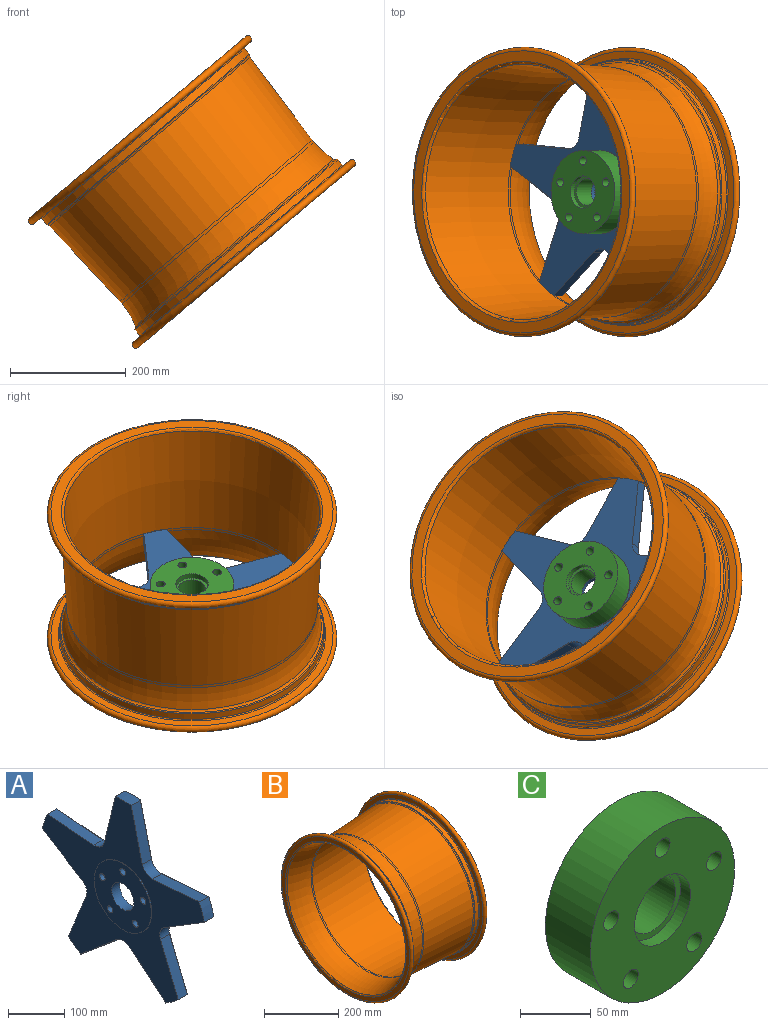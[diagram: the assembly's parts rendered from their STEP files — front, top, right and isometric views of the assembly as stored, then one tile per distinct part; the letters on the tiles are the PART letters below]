
ASSEMBLY  parts=3 mates=5
PART A: 329 faces, bbox 25.4x408.7x389.3 mm
  f0: plane 407.61x388.53mm, normal (1,0,0), area 16823.9mm2, adj f102,f105,f108,f111,f126,f224,f225,f226
  f1: cylinder r=28mm len=56mm, axis (-1,0,0), area 3589mm2, adj f129,f131
  f2: torus R=23mm, axis (1,0,0), area 45.1mm2, adj f3,f4,f18,f26
  f3: cylinder r=2mm len=3.32mm, axis (0,0.31,-0.95), area 8.9mm2, adj f2,f5,f24,f26
  f4: torus R=30mm, axis (1,0,0), area 106.7mm2, adj f2,f6,f23,f26
  f5: torus R=6mm, axis (1,0,0), area 41.3mm2, adj f3,f7,f15,f26
  f6: torus R=23mm, axis (1,0,0), area 45.1mm2, adj f4,f8,f19,f26
  f7: cylinder r=2mm len=101.73mm, axis (0,0.85,0.53), area 371.7mm2, adj f5,f9,f25,f26
  f8: cylinder r=2mm len=3.32mm, axis (0,0.31,-0.95), area 8.9mm2, adj f6,f10,f22,f26
  f9: torus R=6mm, axis (1,0,0), area 29.9mm2, adj f7,f11,f14,f26
  f10: torus R=6mm, axis (1,0,0), area 41.3mm2, adj f8,f12,f16,f26
  f11: torus R=202mm, axis (1,0,0), area 28.8mm2, adj f9,f13,f20,f26
  f12: cylinder r=2mm len=118.12mm, axis (0,-1,-0.08), area 371.7mm2, adj f10,f13,f21,f26
  f13: torus R=6mm, axis (1,0,0), area 29.9mm2, adj f11,f12,f17,f26
  f14: cylinder r=8mm len=9.11mm, axis (1,0,0), area 21mm2, adj f9,f20,f25,f259
  f15: cylinder r=8mm len=11.81mm, axis (-1,0,0), area 29mm2, adj f5,f24,f25,f263
  f16: cylinder r=8mm len=10.45mm, axis (-1,0,0), area 29mm2, adj f10,f21,f22,f256
  f17: cylinder r=8mm len=8.15mm, axis (1,0,0), area 21mm2, adj f13,f20,f21,f255
  f18: cylinder r=25mm len=14.57mm, axis (1,0,0), area 29.6mm2, adj f2,f23,f24,f264
  f19: cylinder r=25mm len=11.94mm, axis (1,0,0), area 29.6mm2, adj f6,f22,f23,f260
  f20: cylinder r=204mm len=8.74mm, axis (1,0,0), area 18.4mm2, adj f11,f14,f17,f257
  f21: plane 117.97x8.92mm, normal (0,0.08,-1), area 236.6mm2, adj f12,f16,f17,f254
  f22: plane 2.7x2mm, normal (0,0.95,0.31), area 5.7mm2, adj f8,f16,f19,f258
  f23: cylinder r=28mm len=29.69mm, axis (1,0,0), area 66.2mm2, adj f4,f18,f19,f262
  f24: plane 2.7x2mm, normal (0,0.95,0.31), area 5.7mm2, adj f3,f15,f18,f265
  f25: plane 100.68x62.12mm, normal (0,-0.53,0.85), area 236.6mm2, adj f7,f14,f15,f261
  f26: plane 132.7x82.52mm, normal (1,0,0), area 5926.3mm2, adj f2,f3,f4,f5,f6,f7,f8,f9
  f27: torus R=23mm, axis (1,0,0), area 45.1mm2, adj f28,f29,f43,f51
  f28: cylinder r=2mm len=3.47mm, axis (0,-0.81,-0.59), area 8.9mm2, adj f27,f30,f49,f51
  f29: torus R=30mm, axis (1,0,0), area 106.7mm2, adj f27,f31,f48,f51
  f30: torus R=6mm, axis (1,0,0), area 41.3mm2, adj f28,f32,f40,f51
  f31: torus R=23mm, axis (1,0,0), area 45.1mm2, adj f29,f33,f44,f51
  f32: cylinder r=2mm len=91.49mm, axis (0,0.76,-0.65), area 371.7mm2, adj f30,f34,f50,f51
  f33: cylinder r=2mm len=3.47mm, axis (0,-0.81,-0.59), area 8.9mm2, adj f31,f35,f47,f51
  f34: torus R=6mm, axis (1,0,0), area 29.9mm2, adj f32,f36,f39,f51
  f35: torus R=6mm, axis (1,0,0), area 41.3mm2, adj f33,f37,f41,f51
  f36: torus R=202mm, axis (1,0,0), area 28.8mm2, adj f34,f38,f45,f51
  f37: cylinder r=2mm len=110.2mm, axis (0,-0.38,0.93), area 371.7mm2, adj f35,f38,f46,f51
  f38: torus R=6mm, axis (1,0,0), area 29.9mm2, adj f36,f37,f42,f51
  f39: cylinder r=8mm len=9.73mm, axis (1,0,0), area 21mm2, adj f34,f45,f50,f271
  f40: cylinder r=8mm len=12.57mm, axis (-1,0,0), area 29mm2, adj f30,f49,f50,f267
  f41: cylinder r=8mm len=12.1mm, axis (-1,0,0), area 29mm2, adj f35,f46,f47,f276
  f42: cylinder r=8mm len=9.4mm, axis (1,0,0), area 21mm2, adj f38,f45,f46,f275
  f43: cylinder r=25mm len=13.77mm, axis (1,0,0), area 29.6mm2, adj f27,f48,f49,f268
  f44: cylinder r=25mm len=11.63mm, axis (1,0,0), area 29.6mm2, adj f31,f47,f48,f272
  f45: cylinder r=204mm len=7.44mm, axis (1,0,0), area 18.4mm2, adj f36,f39,f42,f273
  f46: plane 109.44x44.94mm, normal (0,-0.93,-0.38), area 236.6mm2, adj f37,f41,f42,f277
  f47: plane 2.3x2mm, normal (0,0.59,-0.81), area 5.7mm2, adj f33,f41,f44,f274
  f48: cylinder r=28mm len=25.26mm, axis (1,0,0), area 66.2mm2, adj f29,f43,f44,f270
  f49: plane 2.3x2mm, normal (0,0.59,-0.81), area 5.7mm2, adj f28,f40,f43,f266
  f50: plane 90.19x76.56mm, normal (0,0.65,0.76), area 236.6mm2, adj f32,f39,f40,f269
  f51: plane 126.63x109.34mm, normal (1,0,0), area 5926.3mm2, adj f27,f28,f29,f30,f31,f32,f33,f34
  f52: torus R=23mm, axis (1,0,0), area 45.1mm2, adj f53,f54,f68,f76
  f53: cylinder r=2mm len=3.47mm, axis (0,-0.81,0.59), area 8.9mm2, adj f52,f55,f74,f76
  f54: torus R=30mm, axis (1,0,0), area 106.7mm2, adj f52,f56,f73,f76
  f55: torus R=6mm, axis (1,0,0), area 41.3mm2, adj f53,f57,f65,f76
  f56: torus R=23mm, axis (1,0,0), area 45.1mm2, adj f54,f58,f69,f76
  f57: cylinder r=2mm len=110.2mm, axis (0,-0.38,-0.93), area 371.7mm2, adj f55,f59,f75,f76
  f58: cylinder r=2mm len=3.47mm, axis (0,-0.81,0.59), area 8.9mm2, adj f56,f60,f72,f76
  f59: torus R=6mm, axis (1,0,0), area 29.9mm2, adj f57,f61,f64,f76
  f60: torus R=6mm, axis (1,0,0), area 41.3mm2, adj f58,f62,f66,f76
  f61: torus R=202mm, axis (1,0,0), area 28.8mm2, adj f59,f63,f70,f76
  f62: cylinder r=2mm len=91.49mm, axis (0,0.76,0.65), area 371.7mm2, adj f60,f63,f71,f76
  f63: torus R=6mm, axis (1,0,0), area 29.9mm2, adj f61,f62,f67,f76
  f64: cylinder r=8mm len=9.4mm, axis (1,0,0), area 21mm2, adj f59,f70,f75,f279
  f65: cylinder r=8mm len=12.1mm, axis (-1,0,0), area 29mm2, adj f55,f74,f75,f280
  f66: cylinder r=8mm len=12.57mm, axis (-1,0,0), area 29mm2, adj f60,f71,f72,f287
  f67: cylinder r=8mm len=9.73mm, axis (1,0,0), area 21mm2, adj f63,f70,f71,f283
  f68: cylinder r=25mm len=11.63mm, axis (1,0,0), area 29.6mm2, adj f52,f73,f74,f284
  f69: cylinder r=25mm len=13.77mm, axis (1,0,0), area 29.6mm2, adj f56,f72,f73,f288
  f70: cylinder r=204mm len=7.44mm, axis (1,0,0), area 18.4mm2, adj f61,f64,f67,f281
  f71: plane 90.19x76.56mm, normal (0,-0.65,0.76), area 236.6mm2, adj f62,f66,f67,f285
  f72: plane 2.3x2mm, normal (0,-0.59,-0.81), area 5.7mm2, adj f58,f66,f69,f289
  f73: cylinder r=28mm len=25.26mm, axis (1,0,0), area 66.2mm2, adj f54,f68,f69,f286
  f74: plane 2.3x2mm, normal (0,-0.59,-0.81), area 5.7mm2, adj f53,f65,f68,f282
  f75: plane 109.44x44.94mm, normal (0,0.93,-0.38), area 236.6mm2, adj f57,f64,f65,f278
  f76: plane 126.63x109.34mm, normal (1,0,0), area 5926.3mm2, adj f52,f53,f54,f55,f56,f57,f58,f59
  f77: torus R=23mm, axis (1,0,0), area 45.1mm2, adj f78,f79,f93,f101
  f78: cylinder r=2mm len=3.32mm, axis (0,0.31,0.95), area 8.9mm2, adj f77,f80,f99,f101
  f79: torus R=30mm, axis (1,0,0), area 106.7mm2, adj f77,f81,f98,f101
  f80: torus R=6mm, axis (1,0,0), area 41.3mm2, adj f78,f82,f90,f101
  f81: torus R=23mm, axis (1,0,0), area 45.1mm2, adj f79,f83,f94,f101
  f82: cylinder r=2mm len=118.12mm, axis (0,-1,0.08), area 371.7mm2, adj f80,f84,f100,f101
  f83: cylinder r=2mm len=3.32mm, axis (0,0.31,0.95), area 8.9mm2, adj f81,f85,f97,f101
  f84: torus R=6mm, axis (1,0,0), area 29.9mm2, adj f82,f86,f89,f101
  f85: torus R=6mm, axis (1,0,0), area 41.3mm2, adj f83,f87,f91,f101
  f86: torus R=202mm, axis (1,0,0), area 28.8mm2, adj f84,f88,f95,f101
  f87: cylinder r=2mm len=101.73mm, axis (0,0.85,-0.53), area 371.7mm2, adj f85,f88,f96,f101
  f88: torus R=6mm, axis (1,0,0), area 29.9mm2, adj f86,f87,f92,f101
  f89: cylinder r=8mm len=8.15mm, axis (1,0,0), area 21mm2, adj f84,f95,f100,f291
  f90: cylinder r=8mm len=10.45mm, axis (-1,0,0), area 29mm2, adj f80,f99,f100,f292
  f91: cylinder r=8mm len=11.81mm, axis (-1,0,0), area 29mm2, adj f85,f96,f97,f299
  f92: cylinder r=8mm len=9.11mm, axis (1,0,0), area 21mm2, adj f88,f95,f96,f295
  f93: cylinder r=25mm len=11.94mm, axis (1,0,0), area 29.6mm2, adj f77,f98,f99,f296
  f94: cylinder r=25mm len=14.57mm, axis (1,0,0), area 29.6mm2, adj f81,f97,f98,f300
  f95: cylinder r=204mm len=8.74mm, axis (1,0,0), area 18.4mm2, adj f86,f89,f92,f293
  f96: plane 100.68x62.12mm, normal (0,0.53,0.85), area 236.6mm2, adj f87,f91,f92,f297
  f97: plane 2.7x2mm, normal (0,-0.95,0.31), area 5.7mm2, adj f83,f91,f94,f301
  f98: cylinder r=28mm len=29.69mm, axis (1,0,0), area 66.2mm2, adj f79,f93,f94,f298
  f99: plane 2.7x2mm, normal (0,-0.95,0.31), area 5.7mm2, adj f78,f90,f93,f294
  f100: plane 117.97x8.92mm, normal (0,-0.08,-1), area 236.6mm2, adj f82,f89,f90,f290
  f101: plane 132.7x82.52mm, normal (1,0,0), area 5926.3mm2, adj f77,f78,f79,f80,f81,f82,f83,f84
  f102: cylinder r=209mm len=32.36mm, axis (-1,0,0), area 960.8mm2, adj f0,f104,f106,f127,f168,f316,f317
  f103: plane 100.38x61.94mm, normal (0,0.53,-0.85), area 2712.9mm2, adj f126,f127,f161,f314
  f104: plane 109.11x44.81mm, normal (0,0.93,0.38), area 2712.9mm2, adj f102,f127,f161,f316
  f105: cylinder r=209mm len=32.36mm, axis (-1,0,0), area 960.8mm2, adj f0,f107,f109,f127,f166,f319,f320
  f106: plane 89.92x76.33mm, normal (0,-0.65,-0.76), area 2595mm2, adj f102,f162,f168,f317
  f107: plane 89.92x76.33mm, normal (0,0.65,-0.76), area 2595mm2, adj f105,f162,f166,f319
  f108: cylinder r=209mm len=38.04mm, axis (-1,0,0), area 961mm2, adj f0,f110,f112,f127,f322,f323
  f109: plane 109.11x44.81mm, normal (0,-0.93,0.38), area 2712.9mm2, adj f105,f127,f163,f320
  f110: plane 100.38x61.94mm, normal (0,-0.53,-0.85), area 2712.9mm2, adj f108,f127,f163,f322
  f111: cylinder r=209mm len=40mm, axis (-1,0,0), area 961mm2, adj f0,f113,f127,f134,f325,f326
  f112: plane 117.62x23mm, normal (0,0.08,1), area 2712.9mm2, adj f108,f127,f164,f323
  f113: plane 114.61x27.88mm, normal (0,-0.97,0.24), area 2712.9mm2, adj f111,f127,f164,f325
  f114: cylinder r=18mm len=22.13mm, axis (-1,0,0), area 50.6mm2, adj f192,f193,f214,f243
  f115: cone r=7mm half-angle=30deg, axis (1,0,0), area 596.9mm2, adj f116,f131
  f116: cylinder r=7mm len=14mm, axis (-1,0,0), area 516.3mm2, adj f115,f129
  f117: cylinder r=18mm len=18.82mm, axis (-1,0,0), area 50.6mm2, adj f190,f191,f221,f252
  f118: cone r=7mm half-angle=30deg, axis (1,0,0), area 596.9mm2, adj f119,f131
  f119: cylinder r=7mm len=14mm, axis (-1,0,0), area 516.3mm2, adj f118,f129
  f120: cylinder r=18mm len=18.82mm, axis (-1,0,0), area 50.6mm2, adj f188,f189,f209,f240
  f121: cone r=7mm half-angle=30deg, axis (1,0,0), area 596.9mm2, adj f122,f131
  f122: cylinder r=7mm len=14mm, axis (-1,0,0), area 516.3mm2, adj f121,f129
  f123: cylinder r=18mm len=22.13mm, axis (-1,0,0), area 50.6mm2, adj f186,f187,f197,f228
  f124: cone r=7mm half-angle=30deg, axis (1,0,0), area 596.9mm2, adj f125,f131
  f125: cylinder r=7mm len=14mm, axis (-1,0,0), area 516.3mm2, adj f124,f129
  f126: cylinder r=209mm len=38.04mm, axis (-1,0,0), area 961mm2, adj f0,f103,f127,f135,f314,f328
  f127: plane 408.08x388.53mm, normal (-1,0,0), area 52573.4mm2, adj f102,f103,f104,f105,f108,f109,f110,f111
  f128: cylinder r=72mm len=144mm, axis (-1,0,0), area 633.3mm2, adj f127,f129
  f129: plane 144x144mm, normal (-1,0,0), area 13053.3mm2, adj f1,f116,f119,f122,f125,f128,f133
  f130: cylinder r=18mm len=23.26mm, axis (-1,0,0), area 50.6mm2, adj f184,f185,f202,f231
  f131: plane 143.04x139.91mm, normal (1,0,0), area 9784mm2, adj f1,f115,f118,f121,f124,f132,f194,f195
  f132: cone r=7mm half-angle=30deg, axis (1,0,0), area 596.9mm2, adj f131,f133
  f133: cylinder r=7mm len=14mm, axis (-1,0,0), area 516.3mm2, adj f129,f132
  f134: plane 114.61x27.88mm, normal (0,0.97,0.24), area 2712.9mm2, adj f111,f127,f165,f326
  f135: plane 117.62x23mm, normal (0,-0.08,1), area 2712.9mm2, adj f126,f127,f165,f328
  f136: cylinder r=204mm len=9.19mm, axis (1,0,0), area 18.4mm2, adj f145,f148,f158,f305
  f137: plane 114.95x27.97mm, normal (0,0.97,-0.24), area 236.6mm2, adj f145,f146,f159,f309
  f138: plane 2.84x2mm, normal (0,0,1), area 5.7mm2, adj f143,f146,f155,f313
  f139: cylinder r=28mm len=31.22mm, axis (1,0,0), area 66.2mm2, adj f143,f144,f151,f310
  f140: plane 2.84x2mm, normal (0,0,1), area 5.7mm2, adj f144,f147,f150,f306
  f141: plane 114.95x27.97mm, normal (0,-0.97,-0.24), area 236.6mm2, adj f147,f148,f154,f302
  f142: plane 127x76.77mm, normal (1,0,0), area 5926.3mm2, adj f149,f150,f151,f152,f153,f154,f155,f156
  f143: cylinder r=25mm len=13.94mm, axis (1,0,0), area 29.6mm2, adj f138,f139,f153,f312
  f144: cylinder r=25mm len=13.94mm, axis (1,0,0), area 29.6mm2, adj f139,f140,f149,f308
  f145: cylinder r=8mm len=7.59mm, axis (1,0,0), area 21mm2, adj f136,f137,f160,f307
  f146: cylinder r=8mm len=9.89mm, axis (-1,0,0), area 29mm2, adj f137,f138,f157,f311
  f147: cylinder r=8mm len=9.89mm, axis (-1,0,0), area 29mm2, adj f140,f141,f152,f304
  f148: cylinder r=8mm len=7.59mm, axis (1,0,0), area 21mm2, adj f136,f141,f156,f303
  f149: torus R=23mm, axis (1,0,0), area 45.1mm2, adj f142,f144,f150,f151
  f150: cylinder r=2mm len=2.84mm, axis (0,1,0), area 8.9mm2, adj f140,f142,f149,f152
  f151: torus R=30mm, axis (1,0,0), area 106.7mm2, adj f139,f142,f149,f153
  f152: torus R=6mm, axis (1,0,0), area 41.3mm2, adj f142,f147,f150,f154
  f153: torus R=23mm, axis (1,0,0), area 45.1mm2, adj f142,f143,f151,f155
  f154: cylinder r=2mm len=115.42mm, axis (0,-0.24,0.97), area 371.7mm2, adj f141,f142,f152,f156
  f155: cylinder r=2mm len=2.84mm, axis (0,1,0), area 8.9mm2, adj f138,f142,f153,f157
  f156: torus R=6mm, axis (1,0,0), area 29.9mm2, adj f142,f148,f154,f158
  f157: torus R=6mm, axis (1,0,0), area 41.3mm2, adj f142,f146,f155,f159
  f158: torus R=202mm, axis (1,0,0), area 28.8mm2, adj f136,f142,f156,f160
  f159: cylinder r=2mm len=115.42mm, axis (0,-0.24,-0.97), area 371.7mm2, adj f137,f142,f157,f160
  f160: torus R=6mm, axis (1,0,0), area 29.9mm2, adj f142,f145,f158,f159
  f161: cylinder r=25mm len=30.77mm, axis (1,0,0), area 809.4mm2, adj f103,f104,f127,f315
  f162: cylinder r=25mm len=32.36mm, axis (1,0,0), area 774.2mm2, adj f106,f107,f167,f318
  f163: cylinder r=25mm len=30.77mm, axis (1,0,0), area 809.4mm2, adj f109,f110,f127,f321
  f164: cylinder r=25mm len=26.18mm, axis (1,0,0), area 809.4mm2, adj f112,f113,f127,f324
  f165: cylinder r=25mm len=26.18mm, axis (1,0,0), area 809.4mm2, adj f127,f134,f135,f327
  f166: cylinder r=1mm len=90.83mm, axis (0,-0.76,-0.65), area 185.5mm2, adj f105,f107,f127,f167
  f167: torus R=26mm, axis (1,0,0), area 56.1mm2, adj f127,f162,f166,f168
  f168: cylinder r=1mm len=90.83mm, axis (0,-0.76,0.65), area 185.5mm2, adj f102,f106,f127,f167
  f169: plane 12.5x2mm, normal (0,0,-1), area 25mm2, adj f179,f184,f198,f227
  f170: plane 11.89x3.86mm, normal (0,0.95,-0.31), area 25mm2, adj f179,f187,f194,f224
  f171: plane 11.89x3.86mm, normal (0,0.95,-0.31), area 25mm2, adj f180,f186,f201,f232
  f172: plane 10.11x7.35mm, normal (0,0.59,0.81), area 25mm2, adj f180,f189,f205,f236
  f173: plane 10.11x7.35mm, normal (0,0.59,0.81), area 25mm2, adj f181,f188,f213,f244
  f174: plane 10.11x7.35mm, normal (0,-0.59,0.81), area 25mm2, adj f181,f191,f217,f248
  f175: plane 10.11x7.35mm, normal (0,-0.59,0.81), area 25mm2, adj f182,f190,f222,f251
  f176: plane 11.89x3.86mm, normal (0,-0.95,-0.31), area 25mm2, adj f182,f193,f218,f247
  f177: plane 11.89x3.86mm, normal (0,-0.95,-0.31), area 25mm2, adj f183,f192,f210,f239
  f178: plane 12.5x2mm, normal (0,0,-1), area 25mm2, adj f183,f185,f206,f235
  f179: cylinder r=12mm len=11.41mm, axis (1,0,0), area 30.2mm2, adj f169,f170,f196,f225
  f180: cylinder r=12mm len=13.42mm, axis (1,0,0), area 30.2mm2, adj f171,f172,f203,f234
  f181: cylinder r=12mm len=14.11mm, axis (1,0,0), area 30.2mm2, adj f173,f174,f215,f246
  f182: cylinder r=12mm len=13.42mm, axis (1,0,0), area 30.2mm2, adj f175,f176,f220,f249
  f183: cylinder r=12mm len=11.41mm, axis (1,0,0), area 30.2mm2, adj f177,f178,f208,f237
  f184: cylinder r=20mm len=12.92mm, axis (-1,0,0), area 28.1mm2, adj f130,f169,f200,f229
  f185: cylinder r=20mm len=12.92mm, axis (-1,0,0), area 28.1mm2, adj f130,f178,f204,f233
  f186: cylinder r=20mm len=13.76mm, axis (-1,0,0), area 28.1mm2, adj f123,f171,f199,f230
  f187: cylinder r=20mm len=10.83mm, axis (-1,0,0), area 28.1mm2, adj f123,f170,f195,f226
  f188: cylinder r=20mm len=13.24mm, axis (-1,0,0), area 28.1mm2, adj f120,f173,f211,f242
  f189: cylinder r=20mm len=11.43mm, axis (-1,0,0), area 28.1mm2, adj f120,f172,f207,f238
  f190: cylinder r=20mm len=11.43mm, axis (-1,0,0), area 28.1mm2, adj f117,f175,f223,f253
  f191: cylinder r=20mm len=13.24mm, axis (-1,0,0), area 28.1mm2, adj f117,f174,f219,f250
  f192: cylinder r=20mm len=10.83mm, axis (-1,0,0), area 28.1mm2, adj f114,f177,f212,f241
  f193: cylinder r=20mm len=13.76mm, axis (-1,0,0), area 28.1mm2, adj f114,f176,f216,f245
  f194: cylinder r=2mm len=12.5mm, axis (0,0.31,0.95), area 39.3mm2, adj f131,f170,f195,f196
  f195: torus R=22mm, axis (-1,0,0), area 45.8mm2, adj f131,f187,f194,f197
  f196: torus R=10mm, axis (-1,0,0), area 44.5mm2, adj f131,f179,f194,f198
  f197: torus R=16mm, axis (-1,0,0), area 76.3mm2, adj f123,f131,f195,f199
  f198: cylinder r=2mm len=12.5mm, axis (0,1,0), area 39.3mm2, adj f131,f169,f196,f200
  f199: torus R=22mm, axis (-1,0,0), area 45.8mm2, adj f131,f186,f197,f201
  f200: torus R=22mm, axis (-1,0,0), area 45.8mm2, adj f131,f184,f198,f202
  f201: cylinder r=2mm len=12.5mm, axis (0,0.31,0.95), area 39.3mm2, adj f131,f171,f199,f203
  f202: torus R=16mm, axis (-1,0,0), area 76.3mm2, adj f130,f131,f200,f204
  f203: torus R=10mm, axis (-1,0,0), area 44.5mm2, adj f131,f180,f201,f205
  f204: torus R=22mm, axis (-1,0,0), area 45.8mm2, adj f131,f185,f202,f206
  f205: cylinder r=2mm len=11.29mm, axis (0,-0.81,0.59), area 39.3mm2, adj f131,f172,f203,f207
  f206: cylinder r=2mm len=12.5mm, axis (0,1,0), area 39.3mm2, adj f131,f178,f204,f208
  f207: torus R=22mm, axis (-1,0,0), area 45.8mm2, adj f131,f189,f205,f209
  f208: torus R=10mm, axis (-1,0,0), area 44.5mm2, adj f131,f183,f206,f210
  f209: torus R=16mm, axis (-1,0,0), area 76.3mm2, adj f120,f131,f207,f211
  f210: cylinder r=2mm len=12.5mm, axis (0,0.31,-0.95), area 39.3mm2, adj f131,f177,f208,f212
  f211: torus R=22mm, axis (-1,0,0), area 45.8mm2, adj f131,f188,f209,f213
  f212: torus R=22mm, axis (-1,0,0), area 45.8mm2, adj f131,f192,f210,f214
  f213: cylinder r=2mm len=11.29mm, axis (0,-0.81,0.59), area 39.3mm2, adj f131,f173,f211,f215
  f214: torus R=16mm, axis (-1,0,0), area 76.3mm2, adj f114,f131,f212,f216
  f215: torus R=10mm, axis (-1,0,0), area 44.5mm2, adj f131,f181,f213,f217
  f216: torus R=22mm, axis (-1,0,0), area 45.8mm2, adj f131,f193,f214,f218
  f217: cylinder r=2mm len=11.29mm, axis (0,-0.81,-0.59), area 39.3mm2, adj f131,f174,f215,f219
  f218: cylinder r=2mm len=12.5mm, axis (0,0.31,-0.95), area 39.3mm2, adj f131,f176,f216,f220
  f219: torus R=22mm, axis (-1,0,0), area 45.8mm2, adj f131,f191,f217,f221
  f220: torus R=10mm, axis (-1,0,0), area 44.5mm2, adj f131,f182,f218,f222
  f221: torus R=16mm, axis (-1,0,0), area 76.3mm2, adj f117,f131,f219,f223
  f222: cylinder r=2mm len=11.29mm, axis (0,-0.81,-0.59), area 39.3mm2, adj f131,f175,f220,f223
  f223: torus R=22mm, axis (-1,0,0), area 45.8mm2, adj f131,f190,f221,f222
  f224: cylinder r=1mm len=12.2mm, axis (0,-0.31,-0.95), area 19.6mm2, adj f0,f170,f225,f226
  f225: torus R=13mm, axis (-1,0,0), area 24.4mm2, adj f0,f179,f224,f227
  f226: torus R=19mm, axis (-1,0,0), area 21.7mm2, adj f0,f187,f224,f228
  f227: cylinder r=1mm len=12.5mm, axis (0,-1,0), area 19.6mm2, adj f0,f169,f225,f229
  f228: torus R=19mm, axis (-1,0,0), area 40.5mm2, adj f0,f123,f226,f230
  f229: torus R=19mm, axis (-1,0,0), area 21.7mm2, adj f0,f184,f227,f231
  f230: torus R=19mm, axis (-1,0,0), area 21.7mm2, adj f0,f186,f228,f232
  f231: torus R=19mm, axis (-1,0,0), area 40.5mm2, adj f0,f130,f229,f233
  f232: cylinder r=1mm len=12.2mm, axis (0,-0.31,-0.95), area 19.6mm2, adj f0,f171,f230,f234
  f233: torus R=19mm, axis (-1,0,0), area 21.7mm2, adj f0,f185,f231,f235
  f234: torus R=13mm, axis (-1,0,0), area 24.4mm2, adj f0,f180,f232,f236
  f235: cylinder r=1mm len=12.5mm, axis (0,-1,0), area 19.6mm2, adj f0,f178,f233,f237
  f236: cylinder r=1mm len=10.7mm, axis (0,0.81,-0.59), area 19.6mm2, adj f0,f172,f234,f238
  f237: torus R=13mm, axis (-1,0,0), area 24.4mm2, adj f0,f183,f235,f239
  f238: torus R=19mm, axis (-1,0,0), area 21.7mm2, adj f0,f189,f236,f240
  f239: cylinder r=1mm len=12.2mm, axis (0,-0.31,0.95), area 19.6mm2, adj f0,f177,f237,f241
  f240: torus R=19mm, axis (-1,0,0), area 40.5mm2, adj f0,f120,f238,f242
  f241: torus R=19mm, axis (-1,0,0), area 21.7mm2, adj f0,f192,f239,f243
  f242: torus R=19mm, axis (-1,0,0), area 21.7mm2, adj f0,f188,f240,f244
  f243: torus R=19mm, axis (-1,0,0), area 40.5mm2, adj f0,f114,f241,f245
  f244: cylinder r=1mm len=10.7mm, axis (0,0.81,-0.59), area 19.6mm2, adj f0,f173,f242,f246
  f245: torus R=19mm, axis (-1,0,0), area 21.7mm2, adj f0,f193,f243,f247
  f246: torus R=13mm, axis (-1,0,0), area 24.4mm2, adj f0,f181,f244,f248
  f247: cylinder r=1mm len=12.2mm, axis (0,-0.31,0.95), area 19.6mm2, adj f0,f176,f245,f249
  f248: cylinder r=1mm len=10.7mm, axis (0,0.81,0.59), area 19.6mm2, adj f0,f174,f246,f250
  f249: torus R=13mm, axis (-1,0,0), area 24.4mm2, adj f0,f182,f247,f251
  f250: torus R=19mm, axis (-1,0,0), area 21.7mm2, adj f0,f191,f248,f252
  f251: cylinder r=1mm len=10.7mm, axis (0,0.81,0.59), area 19.6mm2, adj f0,f175,f249,f253
  f252: torus R=19mm, axis (-1,0,0), area 40.5mm2, adj f0,f117,f250,f253
  f253: torus R=19mm, axis (-1,0,0), area 21.7mm2, adj f0,f190,f251,f252
  f254: cylinder r=1mm len=118.04mm, axis (0,-1,-0.08), area 185.8mm2, adj f0,f21,f255,f256
  f255: torus R=9mm, axis (-1,0,0), area 17.2mm2, adj f0,f17,f254,f257
  f256: torus R=9mm, axis (-1,0,0), area 23.8mm2, adj f0,f16,f254,f258
  f257: torus R=205mm, axis (-1,0,0), area 14.5mm2, adj f0,f20,f255,f259
  f258: cylinder r=1mm len=3.01mm, axis (0,0.31,-0.95), area 4.5mm2, adj f0,f22,f256,f260
  f259: torus R=9mm, axis (-1,0,0), area 17.2mm2, adj f0,f14,f257,f261
  f260: torus R=26mm, axis (-1,0,0), area 23.6mm2, adj f0,f19,f258,f262
  f261: cylinder r=1mm len=101.21mm, axis (0,0.85,0.53), area 185.8mm2, adj f0,f25,f259,f263
  f262: torus R=27mm, axis (-1,0,0), area 51.3mm2, adj f0,f23,f260,f264
  f263: torus R=9mm, axis (-1,0,0), area 23.8mm2, adj f0,f15,f261,f265
  f264: torus R=26mm, axis (-1,0,0), area 23.6mm2, adj f0,f18,f262,f265
  f265: cylinder r=1mm len=3.01mm, axis (0,0.31,-0.95), area 4.5mm2, adj f0,f24,f263,f264
  f266: cylinder r=1mm len=2.88mm, axis (0,-0.81,-0.59), area 4.5mm2, adj f0,f49,f267,f268
  f267: torus R=9mm, axis (-1,0,0), area 23.8mm2, adj f0,f40,f266,f269
  f268: torus R=26mm, axis (-1,0,0), area 23.6mm2, adj f0,f43,f266,f270
  f269: cylinder r=1mm len=90.84mm, axis (0,0.76,-0.65), area 185.8mm2, adj f0,f50,f267,f271
  f270: torus R=27mm, axis (-1,0,0), area 51.3mm2, adj f0,f48,f268,f272
  f271: torus R=9mm, axis (-1,0,0), area 17.2mm2, adj f0,f39,f269,f273
  f272: torus R=26mm, axis (-1,0,0), area 23.6mm2, adj f0,f44,f270,f274
  f273: torus R=205mm, axis (-1,0,0), area 14.5mm2, adj f0,f45,f271,f275
  f274: cylinder r=1mm len=2.88mm, axis (0,-0.81,-0.59), area 4.5mm2, adj f0,f47,f272,f276
  f275: torus R=9mm, axis (-1,0,0), area 17.2mm2, adj f0,f42,f273,f277
  f276: torus R=9mm, axis (-1,0,0), area 23.8mm2, adj f0,f41,f274,f277
  f277: cylinder r=1mm len=109.82mm, axis (0,-0.38,0.93), area 185.8mm2, adj f0,f46,f275,f276
  f278: cylinder r=1mm len=109.82mm, axis (0,-0.38,-0.93), area 185.8mm2, adj f0,f75,f279,f280
  f279: torus R=9mm, axis (-1,0,0), area 17.2mm2, adj f0,f64,f278,f281
  f280: torus R=9mm, axis (-1,0,0), area 23.8mm2, adj f0,f65,f278,f282
  f281: torus R=205mm, axis (-1,0,0), area 14.5mm2, adj f0,f70,f279,f283
  f282: cylinder r=1mm len=2.88mm, axis (0,-0.81,0.59), area 4.5mm2, adj f0,f74,f280,f284
  f283: torus R=9mm, axis (-1,0,0), area 17.2mm2, adj f0,f67,f281,f285
  f284: torus R=26mm, axis (-1,0,0), area 23.6mm2, adj f0,f68,f282,f286
  f285: cylinder r=1mm len=90.84mm, axis (0,0.76,0.65), area 185.8mm2, adj f0,f71,f283,f287
  f286: torus R=27mm, axis (-1,0,0), area 51.3mm2, adj f0,f73,f284,f288
  f287: torus R=9mm, axis (-1,0,0), area 23.8mm2, adj f0,f66,f285,f289
  f288: torus R=26mm, axis (-1,0,0), area 23.6mm2, adj f0,f69,f286,f289
  f289: cylinder r=1mm len=2.88mm, axis (0,-0.81,0.59), area 4.5mm2, adj f0,f72,f287,f288
  f290: cylinder r=1mm len=118.04mm, axis (0,-1,0.08), area 185.8mm2, adj f0,f100,f291,f292
  f291: torus R=9mm, axis (-1,0,0), area 17.2mm2, adj f0,f89,f290,f293
  f292: torus R=9mm, axis (-1,0,0), area 23.8mm2, adj f0,f90,f290,f294
  f293: torus R=205mm, axis (-1,0,0), area 14.5mm2, adj f0,f95,f291,f295
  f294: cylinder r=1mm len=3.01mm, axis (0,0.31,0.95), area 4.5mm2, adj f0,f99,f292,f296
  f295: torus R=9mm, axis (-1,0,0), area 17.2mm2, adj f0,f92,f293,f297
  f296: torus R=26mm, axis (-1,0,0), area 23.6mm2, adj f0,f93,f294,f298
  f297: cylinder r=1mm len=101.21mm, axis (0,0.85,-0.53), area 185.8mm2, adj f0,f96,f295,f299
  f298: torus R=27mm, axis (-1,0,0), area 51.3mm2, adj f0,f98,f296,f300
  f299: torus R=9mm, axis (-1,0,0), area 23.8mm2, adj f0,f91,f297,f301
  f300: torus R=26mm, axis (-1,0,0), area 23.6mm2, adj f0,f94,f298,f301
  f301: cylinder r=1mm len=3.01mm, axis (0,0.31,0.95), area 4.5mm2, adj f0,f97,f299,f300
  f302: cylinder r=1mm len=115.19mm, axis (0,-0.24,0.97), area 185.8mm2, adj f0,f141,f303,f304
  f303: torus R=9mm, axis (-1,0,0), area 17.2mm2, adj f0,f148,f302,f305
  f304: torus R=9mm, axis (-1,0,0), area 23.8mm2, adj f0,f147,f302,f306
  f305: torus R=205mm, axis (-1,0,0), area 14.5mm2, adj f0,f136,f303,f307
  f306: cylinder r=1mm len=2.84mm, axis (0,1,0), area 4.5mm2, adj f0,f140,f304,f308
  f307: torus R=9mm, axis (-1,0,0), area 17.2mm2, adj f0,f145,f305,f309
  f308: torus R=26mm, axis (-1,0,0), area 23.6mm2, adj f0,f144,f306,f310
  f309: cylinder r=1mm len=115.19mm, axis (0,-0.24,-0.97), area 185.8mm2, adj f0,f137,f307,f311
  f310: torus R=27mm, axis (-1,0,0), area 51.3mm2, adj f0,f139,f308,f312
  f311: torus R=9mm, axis (-1,0,0), area 23.8mm2, adj f0,f146,f309,f313
  f312: torus R=26mm, axis (-1,0,0), area 23.6mm2, adj f0,f143,f310,f313
  f313: cylinder r=1mm len=2.84mm, axis (0,1,0), area 4.5mm2, adj f0,f138,f311,f312
  f314: cylinder r=1mm len=101.2mm, axis (0,0.85,0.53), area 185.5mm2, adj f0,f103,f126,f315
  f315: torus R=26mm, axis (-1,0,0), area 56.1mm2, adj f0,f161,f314,f316
  f316: cylinder r=1mm len=109.81mm, axis (0,-0.38,0.93), area 185.5mm2, adj f0,f102,f104,f315
  f317: cylinder r=1mm len=90.83mm, axis (0,0.76,-0.65), area 185.5mm2, adj f0,f102,f106,f318
  f318: torus R=26mm, axis (-1,0,0), area 56.1mm2, adj f0,f162,f317,f319
  f319: cylinder r=1mm len=90.83mm, axis (0,0.76,0.65), area 185.5mm2, adj f0,f105,f107,f318
  f320: cylinder r=1mm len=109.81mm, axis (0,-0.38,-0.93), area 185.5mm2, adj f0,f105,f109,f321
  f321: torus R=26mm, axis (-1,0,0), area 56.1mm2, adj f0,f163,f320,f322
  f322: cylinder r=1mm len=101.2mm, axis (0,0.85,-0.53), area 185.5mm2, adj f0,f108,f110,f321
  f323: cylinder r=1mm len=118.04mm, axis (0,-1,0.08), area 185.5mm2, adj f0,f108,f112,f324
  f324: torus R=26mm, axis (-1,0,0), area 56.1mm2, adj f0,f164,f323,f325
  f325: cylinder r=1mm len=115.18mm, axis (0,-0.24,-0.97), area 185.5mm2, adj f0,f111,f113,f324
  f326: cylinder r=1mm len=115.18mm, axis (0,-0.24,0.97), area 185.5mm2, adj f0,f111,f134,f327
  f327: torus R=26mm, axis (-1,0,0), area 56.1mm2, adj f0,f165,f326,f328
  f328: cylinder r=1mm len=118.04mm, axis (0,-1,-0.08), area 185.5mm2, adj f0,f126,f135,f327
PART B: 22 faces, bbox 1290.3x1501.8x1501.8 mm
  f0: cylinder r=216.6mm len=433.2mm, axis (-1,0,0), area 6804.7mm2, adj f1,f13
  f1: torus R=363.55mm, axis (-1,0,0), area 61214.5mm2, adj f0,f16
  f2: cylinder r=228.6mm len=457.2mm, axis (-1,0,0), area 17458.6mm2, adj f18,f19
  f3: plane 487.2x487.2mm, normal (1,0,0), area 19366.7mm2, adj f4,f19
  f4: torus R=243.6mm, axis (-1,0,0), area 30543.8mm2, adj f3,f5
  f5: plane 487.2x487.2mm, normal (-1,0,0), area 19858.2mm2, adj f4,f14
  f6: torus R=363.55mm, axis (-1,0,0), area 102319.1mm2, adj f7,f14
  f7: cylinder r=207.6mm len=415.2mm, axis (-1,0,0), area 6521.9mm2, adj f6,f8
  f8: torus R=1861.88mm, axis (-1,0,0), area 275638.2mm2, adj f7,f15
  f9: plane 487.2x487.2mm, normal (1,0,0), area 26679mm2, adj f10,f15
  f10: torus R=243.6mm, axis (-1,0,0), area 30543.8mm2, adj f9,f11
  f11: plane 487.2x487.2mm, normal (-1,0,0), area 19366.7mm2, adj f10,f20
  f12: cylinder r=228.6mm len=457.2mm, axis (-1,0,0), area 18703.2mm2, adj f20,f21
  f13: torus R=1861.88mm, axis (-1,0,0), area 247312.2mm2, adj f0,f17
  f14: torus R=230.26mm, axis (-1,0,0), area 7745.3mm2, adj f5,f6
  f15: torus R=225.5mm, axis (-1,0,0), area 10103.8mm2, adj f8,f9
  f16: torus R=228.06mm, axis (-1,0,0), area 7466.7mm2, adj f1,f18
  f17: torus R=231.3mm, axis (-1,0,0), area 5171.8mm2, adj f13,f21
  f18: torus R=226.6mm, axis (1,0,0), area 3897.2mm2, adj f2,f16
  f19: torus R=230.6mm, axis (1,0,0), area 4526.7mm2, adj f2,f3
  f20: torus R=230.6mm, axis (1,0,0), area 4526.7mm2, adj f11,f12
  f21: torus R=226.6mm, axis (1,0,0), area 2394.1mm2, adj f12,f17
PART C: 14 faces, bbox 144x50x144 mm
  f0: cylinder r=23mm len=46mm, axis (0,-1,0), area 5780.5mm2, adj f10,f12
  f1: cylinder r=7.5mm len=45mm, axis (0,-1,0), area 2120.6mm2, adj f6,f7
  f2: cylinder r=7.5mm len=45mm, axis (0,-1,0), area 2120.6mm2, adj f6,f7
  f3: cylinder r=7.5mm len=45mm, axis (0,-1,0), area 2120.6mm2, adj f6,f7
  f4: cylinder r=7.5mm len=45mm, axis (0,-1,0), area 2120.6mm2, adj f6,f7
  f5: cylinder r=72mm len=144mm, axis (0,1,0), area 20357.5mm2, adj f6,f7
  f6: plane 144x144mm, normal (0,-1,0), area 12939.4mm2, adj f1,f2,f3,f4,f5,f8,f9
  f7: plane 144x144mm, normal (0,1,0), area 12939.4mm2, adj f1,f2,f3,f4,f5,f8,f11
  f8: cylinder r=7.5mm len=45mm, axis (0,-1,0), area 2120.6mm2, adj f6,f7
  f9: cylinder r=28mm len=56mm, axis (0,-1,0), area 1759.3mm2, adj f6,f10
  f10: plane 56x56mm, normal (0,-1,0), area 801.1mm2, adj f0,f9
  f11: cylinder r=28mm len=56mm, axis (0,-1,0), area 527.8mm2, adj f7,f13
  f12: plane 52x52mm, normal (0,1,0), area 461.8mm2, adj f0,f13
  f13: torus R=26mm, axis (0,1,0), area 538.4mm2, adj f11,f12
PLACE A rot(axis=(-0.32,0.94,0.15),52.9deg) t=(323.92,-140.41,310.86)mm
PLACE B rot(axis=(0,-1,0),130deg) t=(283.2,-140.41,359.39)mm
PLACE C rot(axis=(-0.89,-0.32,-0.32),96.7deg) t=(323.92,-140.41,310.86)mm
MATE cylindrical C.f9 <-> B.f0  axis (-0.64,0,0.77) through (298.21,-140.41,341.5)mm
MATE planar C.f5 <-> B.f0  axis (-0.64,0,0.77) through (294.99,-140.41,345.33)mm
MATE cylindrical C.f11 <-> A.f1  axis (-0.64,0,0.77) through (324.88,-140.41,309.71)mm
MATE cylindrical C.f4 <-> A.f130  axis (-0.64,0,0.77) through (363.26,-123.72,343.87)mm
MATE planar A.f1 <-> C.f5  axis (-0.64,0,0.77) through (323.92,-140.41,310.86)mm
